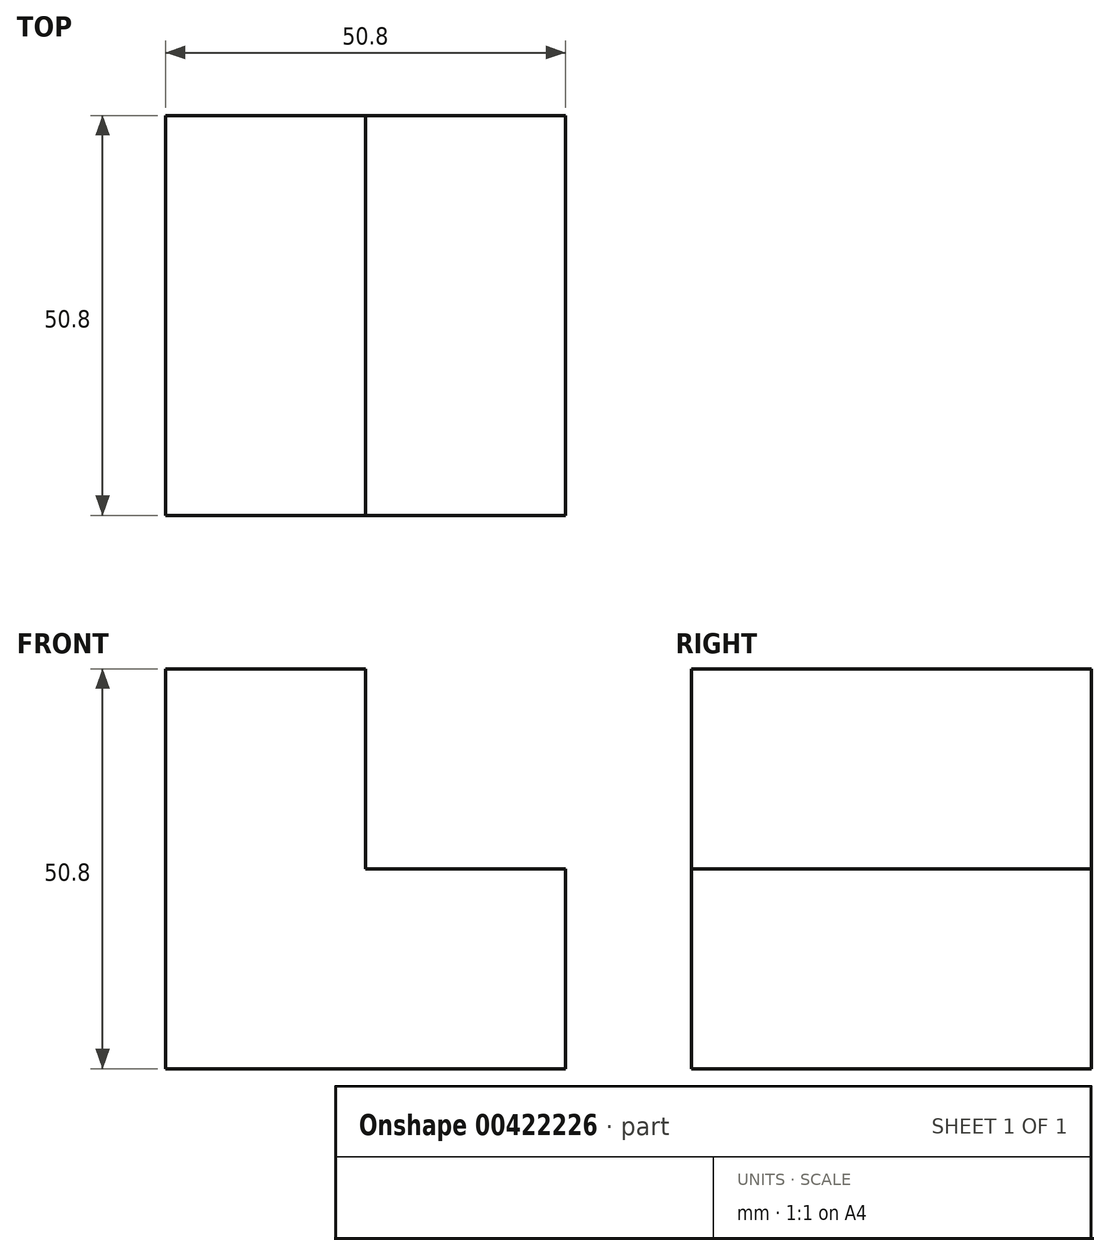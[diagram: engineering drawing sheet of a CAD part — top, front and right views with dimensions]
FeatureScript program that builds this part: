
annotation { "Feature Type Name" : "Feature", "Feature Type Description" : "" }
export const myFeature = defineFeature(function(context is Context, id is Id, definition is map)
    precondition{}
    {
        {
            var Q0;
            Q0=qCreatedBy(makeId("Front.planeOp"),FACE);
            var sketch = newSketch(context, id + "F0", { "sketchPlane" : qUnion([Q0])});
            skLineSegment(sketch, "E0", {"start": v(0, 0) * mm, "end": v(0, 50.8) * mm});
            skLineSegment(sketch, "E1", {"start": v(0, 50.8) * mm, "end": v(25.4, 50.8) * mm});
            skLineSegment(sketch, "E2", {"start": v(25.4, 50.8) * mm, "end": v(25.4, 25.4) * mm});
            skLineSegment(sketch, "E3", {"start": v(25.4, 25.4) * mm, "end": v(50.8, 25.4) * mm});
            skLineSegment(sketch, "E4", {"start": v(50.8, 25.4) * mm, "end": v(50.8, 0) * mm});
            skLineSegment(sketch, "E5", {"start": v(0, 0) * mm, "end": v(50.8, 0) * mm});
            skLineSegment(sketch, "E6", {"start": v(50.8, 0) * mm, "end": v(50.8, 0) * mm});
            skSolve(sketch);
        }
        {
            var Q0;
            Q0 = qSketchRegion(id + "F0", true);
            extrude(context, id + "F1", {"entities" : qUnion([Q0]), "depth" : 50.8 * mm});
        }
    });
